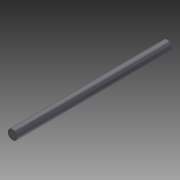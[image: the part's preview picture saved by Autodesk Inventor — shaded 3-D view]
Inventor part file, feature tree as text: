
AUTODESK INVENTOR PART (.ipt)
format: ipt  version: 2014 SP1 (Build 180222100, 222)  size: 69,120 bytes
history: native  units: in
note: dims shown in document units (in); Inventor stores cm internally (conversion verified against a paired STEP export)
features: extrude x1, sketch x1
ambient origin geometry x8: Origin, YZ Plane, XZ Plane, XY Plane, X Axis, Y Axis, Z Axis, Center Point
bodies: Solid1 (feature_tree)
feature tree (2):
  extrude  "Extrusion1"  Depth=4.0in TaperAngle=0.0deg
  sketch  "Sketch1"  dims[d0=0.25in d1=4.0in d2=0.0in]
